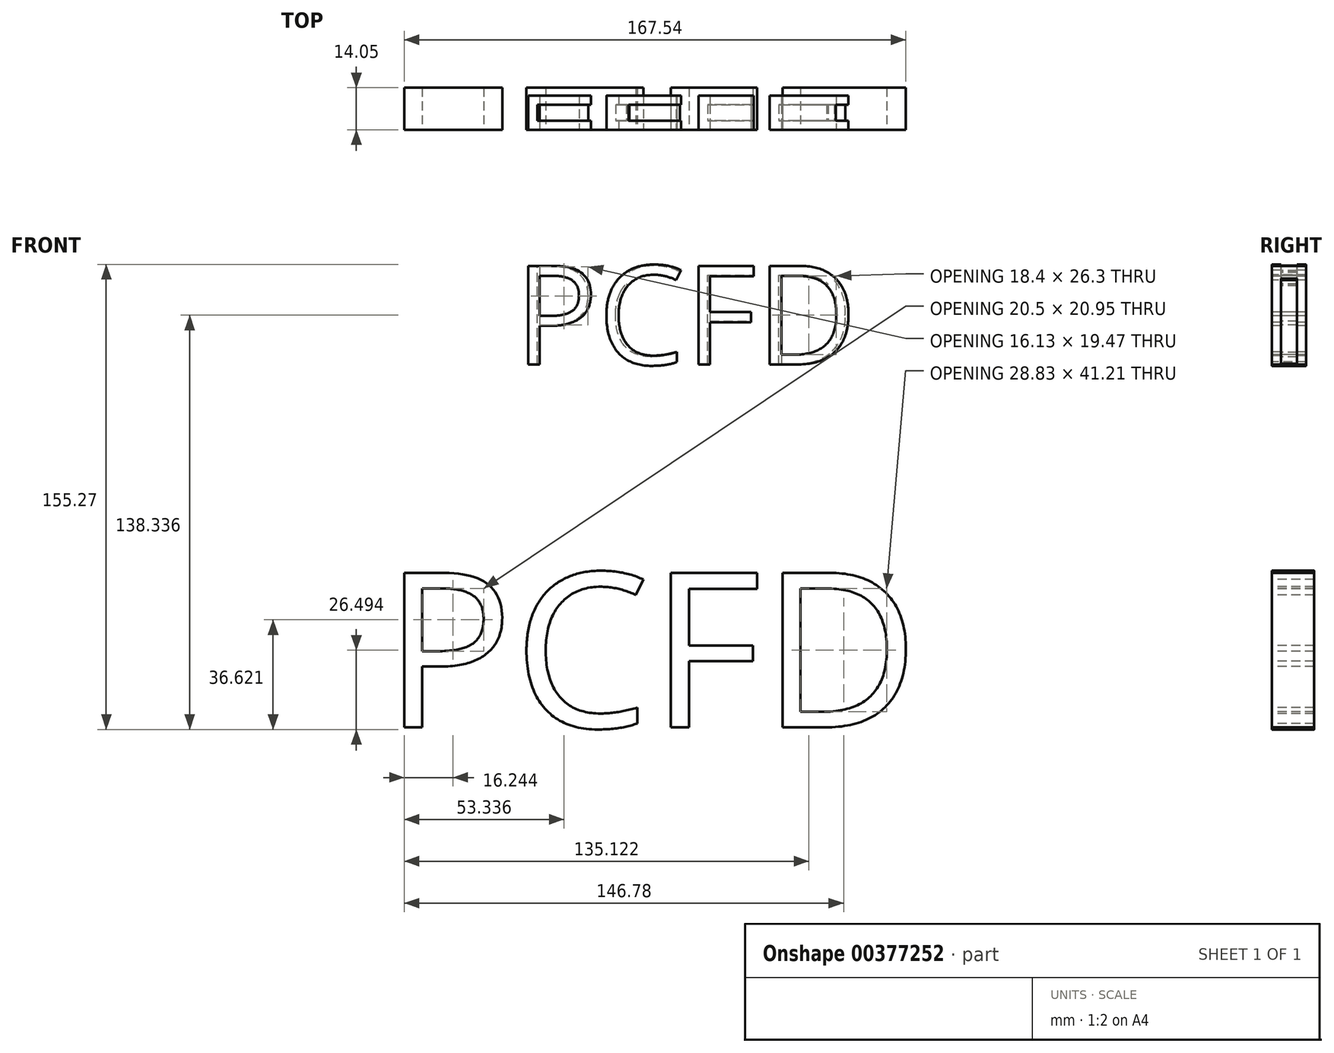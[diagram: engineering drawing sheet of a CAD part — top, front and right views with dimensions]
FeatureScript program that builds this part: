
annotation { "Feature Type Name" : "Feature", "Feature Type Description" : "" }
export const myFeature = defineFeature(function(context is Context, id is Id, definition is map)
    precondition{}
    {
        {
            var Q0;
            Q0=qCreatedBy(makeId("Front.planeOp"),FACE);
            var sketch = newSketch(context, id + "F0", { "sketchPlane" : qUnion([Q0])});
            skText(sketch, "E0", { "text": "PCFD", "fontName": "OpenSans-Regular.ttf"});
            const initialGuessF0  = {"E0": [-0.11447, 0.0936, 1, 0, 0.0332]};
            skSetInitialGuess(sketch, initialGuessF0);
            skSolve(sketch);
        }
        {
            var Q0;
            Q0 = qSketchRegion(id + "F0", true);
            extrude(context, id + "F1", {"entities" : qUnion([Q0]), "oppositeDirection" : true, "depth" : 11.38 * mm});
        }
        {
            var Q0;
            Q0=makeQuery(id+"F1.opExtrude","SWEPT_FACE",FACE,{"disambiguationData":[OSD([sQuery(id+"F0.wireOp",EDGE,"E0.sketch_text.stroke-0")])]});
            var Q1;
            Q1=makeQuery(id+"F1.opExtrude","SWEPT_FACE",FACE,{"disambiguationData":[OSD([sQuery(id+"F0.wireOp",EDGE,"E0.sketch_text.stroke-1")])]});
            var Q2;
            Q2=makeQuery(id+"F1.opExtrude","SWEPT_FACE",FACE,{"disambiguationData":[OSD([sQuery(id+"F0.wireOp",EDGE,"E0.sketch_text.stroke-2")])]});
            var Q3;
            Q3=makeQuery(id+"F1.opExtrude","SWEPT_FACE",FACE,{"disambiguationData":[OSD([sQuery(id+"F0.wireOp",EDGE,"E0.sketch_text.stroke-3")])]});
            var Q4;
            Q4=makeQuery(id+"F1.opExtrude","SWEPT_FACE",FACE,{"disambiguationData":[OSD([sQuery(id+"F0.wireOp",EDGE,"E0.sketch_text.stroke-14")])]});
            var Q5;
            Q5=makeQuery(id+"F1.opExtrude","SWEPT_FACE",FACE,{"disambiguationData":[OSD([sQuery(id+"F0.wireOp",EDGE,"E0.sketch_text.stroke-4")])]});
            var Q6;
            Q6=makeQuery(id+"F1.opExtrude","SWEPT_FACE",FACE,{"disambiguationData":[OSD([sQuery(id+"F0.wireOp",EDGE,"E0.sketch_text.stroke-7")])]});
            var Q7;
            Q7=makeQuery(id+"F1.opExtrude","SWEPT_FACE",FACE,{"disambiguationData":[OSD([sQuery(id+"F0.wireOp",EDGE,"E0.sketch_text.stroke-6")])]});
            var Q8;
            Q8=makeQuery(id+"F1.opExtrude","SWEPT_FACE",FACE,{"disambiguationData":[OSD([sQuery(id+"F0.wireOp",EDGE,"E0.sketch_text.stroke-17")])]});
            var Q9;
            Q9=makeQuery(id+"F1.opExtrude","SWEPT_FACE",FACE,{"disambiguationData":[OSD([sQuery(id+"F0.wireOp",EDGE,"E0.sketch_text.stroke-18")])]});
            var Q10;
            Q10=makeQuery(id+"F1.opExtrude","SWEPT_FACE",FACE,{"disambiguationData":[OSD([sQuery(id+"F0.wireOp",EDGE,"E0.sketch_text.stroke-27")])]});
            var Q11;
            Q11=makeQuery(id+"F1.opExtrude","SWEPT_FACE",FACE,{"disambiguationData":[OSD([sQuery(id+"F0.wireOp",EDGE,"E0.sketch_text.stroke-16")])]});
            var Q12;
            Q12=makeQuery(id+"F1.opExtrude","SWEPT_FACE",FACE,{"disambiguationData":[OSD([sQuery(id+"F0.wireOp",EDGE,"E0.sketch_text.stroke-28")])]});
            var Q13;
            Q13=makeQuery(id+"F1.opExtrude","SWEPT_FACE",FACE,{"disambiguationData":[OSD([sQuery(id+"F0.wireOp",EDGE,"E0.sketch_text.stroke-19")])]});
            var Q14;
            Q14=makeQuery(id+"F1.opExtrude","SWEPT_FACE",FACE,{"disambiguationData":[OSD([sQuery(id+"F0.wireOp",EDGE,"E0.sketch_text.stroke-20")])]});
            var Q15;
            Q15=makeQuery(id+"F1.opExtrude","SWEPT_FACE",FACE,{"disambiguationData":[OSD([sQuery(id+"F0.wireOp",EDGE,"E0.sketch_text.stroke-26")])]});
            var Q16;
            Q16=makeQuery(id+"F1.opExtrude","SWEPT_FACE",FACE,{"disambiguationData":[OSD([sQuery(id+"F0.wireOp",EDGE,"E0.sketch_text.stroke-41")])]});
            var Q17;
            Q17=makeQuery(id+"F1.opExtrude","SWEPT_FACE",FACE,{"disambiguationData":[OSD([sQuery(id+"F0.wireOp",EDGE,"E0.sketch_text.stroke-40")])]});
            var Q18;
            Q18=makeQuery(id+"F1.opExtrude","SWEPT_FACE",FACE,{"disambiguationData":[OSD([sQuery(id+"F0.wireOp",EDGE,"E0.sketch_text.stroke-42")])]});
            var Q19;
            Q19=makeQuery(id+"F1.opExtrude","SWEPT_FACE",FACE,{"disambiguationData":[OSD([sQuery(id+"F0.wireOp",EDGE,"E0.sketch_text.stroke-48")])]});
            var Q20;
            Q20=makeQuery(id+"F1.opExtrude","SWEPT_FACE",FACE,{"disambiguationData":[OSD([sQuery(id+"F0.wireOp",EDGE,"E0.sketch_text.stroke-49")])]});
            var Q21;
            Q21=makeQuery(id+"F1.opExtrude","SWEPT_FACE",FACE,{"disambiguationData":[OSD([sQuery(id+"F0.wireOp",EDGE,"E0.sketch_text.stroke-39")])]});
            var Q22;
            Q22=makeQuery(id+"F1.opExtrude","SWEPT_FACE",FACE,{"disambiguationData":[OSD([sQuery(id+"F0.wireOp",EDGE,"E0.sketch_text.stroke-35")])]});
            var Q23;
            Q23=makeQuery(id+"F1.opExtrude","SWEPT_FACE",FACE,{"disambiguationData":[OSD([sQuery(id+"F0.wireOp",EDGE,"E0.sketch_text.stroke-34")])]});
            var Q24;
            Q24=makeQuery(id+"F1.opExtrude","SWEPT_FACE",FACE,{"disambiguationData":[OSD([sQuery(id+"F0.wireOp",EDGE,"E0.sketch_text.stroke-38")])]});
            var Q25;
            Q25=makeQuery(id+"F1.opExtrude","SWEPT_FACE",FACE,{"disambiguationData":[OSD([sQuery(id+"F0.wireOp",EDGE,"E0.sketch_text.stroke-37")])]});
            var Q26;
            Q26=makeQuery(id+"F1.opExtrude","SWEPT_FACE",FACE,{"disambiguationData":[OSD([sQuery(id+"F0.wireOp",EDGE,"E0.sketch_text.stroke-50")])]});
            var Q27;
            Q27=makeQuery(id+"F1.opExtrude","SWEPT_FACE",FACE,{"disambiguationData":[OSD([sQuery(id+"F0.wireOp",EDGE,"E0.sketch_text.stroke-30")])]});
            var Q28;
            Q28=makeQuery(id+"F1.opExtrude","SWEPT_FACE",FACE,{"disambiguationData":[OSD([sQuery(id+"F0.wireOp",EDGE,"E0.sketch_text.stroke-33")])]});
            var Q29;
            Q29=makeQuery(id+"F1.opExtrude","SWEPT_FACE",FACE,{"disambiguationData":[OSD([sQuery(id+"F0.wireOp",EDGE,"E0.sketch_text.stroke-46")])]});
            shell(context, id + "F2", {"entities" : qUnion([Q0, Q1, Q2, Q3, Q4, Q5, Q6, Q7, Q8, Q9, Q10, Q11, Q12, Q13, Q14, Q15, Q16, Q17, Q18, Q19, Q20, Q21, Q22, Q23, Q24, Q25, Q26, Q27, Q28, Q29]), "thickness" : 3.05 * mm});
        }
        {
            var Q0;
            Q0=qCreatedBy(makeId("Front.planeOp"),FACE);
            var sketch = newSketch(context, id + "F3", { "sketchPlane" : qUnion([Q0])});
            skText(sketch, "E1", { "text": "PCFD", "fontName": "OpenSans-Regular.ttf"});
            const initialGuessF3  = {"E1": [-0.15848, -0.02757, 1, 0, 0.05202]};
            skSetInitialGuess(sketch, initialGuessF3);
            skSolve(sketch);
        }
        {
            var Q0;
            Q0 = qSketchRegion(id + "F3", true);
            extrude(context, id + "F4", {"entities" : qUnion([Q0]), "oppositeDirection" : true, "depth" : 14.05 * mm});
        }
    });
